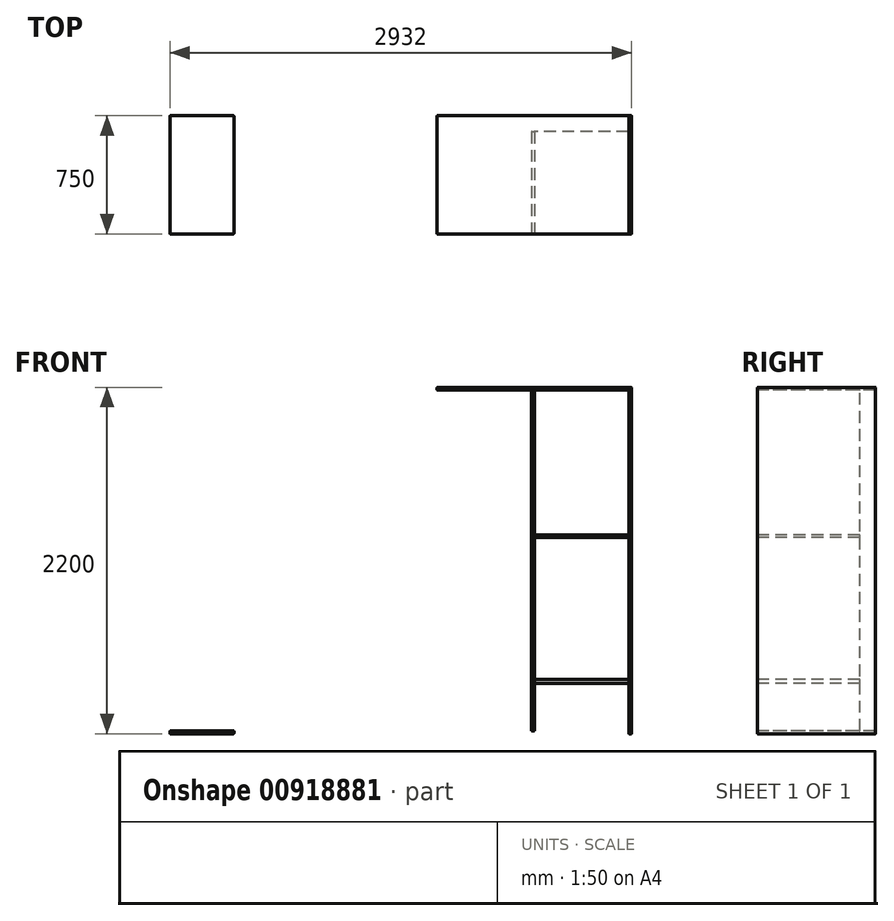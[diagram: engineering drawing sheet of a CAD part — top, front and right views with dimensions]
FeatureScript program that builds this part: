
annotation { "Feature Type Name" : "Feature", "Feature Type Description" : "" }
export const myFeature = defineFeature(function(context is Context, id is Id, definition is map)
    precondition{}
    {
        {
            var Q0;
            Q0=qCreatedBy(makeId("Front.planeOp"),FACE);
            var sketch = newSketch(context, id + "F0", { "sketchPlane" : qUnion([Q0])});
            skLineSegment(sketch, "E0.right", {"start": v(2950, 0) * mm, "end": v(2950, 2200) * mm});
            skLineSegment(sketch, "E1", {"start": v(1714, 2200) * mm, "end": v(1714, 0) * mm});
            skLineSegment(sketch, "E2", {"start": v(2332, 18) * mm, "end": v(2332, 2182) * mm});
            skLineSegment(sketch, "E3", {"start": v(1696, 0) * mm, "end": v(1696, 2200) * mm});
            skLineSegment(sketch, "E4", {"start": v(2932, 0) * mm, "end": v(2932, 2200) * mm});
            skLineSegment(sketch, "E5", {"start": v(2314, 18) * mm, "end": v(2314, 2182) * mm});
            skLineSegment(sketch, "E6", {"start": v(2932, 2200) * mm, "end": v(2950, 2200) * mm});
            skLineSegment(sketch, "E7", {"start": v(2932, 18) * mm, "end": v(1714, 18) * mm});
            skLineSegment(sketch, "E8", {"start": v(1714, 0) * mm, "end": v(2932, 0) * mm});
            skLineSegment(sketch, "E9", {"start": v(2932, 2200) * mm, "end": v(1714, 2200) * mm});
            skLineSegment(sketch, "E10", {"start": v(1714, 2182) * mm, "end": v(2932, 2182) * mm});
            skLineSegment(sketch, "E11", {"start": v(1714, 2200) * mm, "end": v(1696, 2200) * mm});
            skLineSegment(sketch, "E12", {"start": v(1714, 0) * mm, "end": v(1696, 0) * mm});
            skLineSegment(sketch, "E13", {"start": v(2932, 0) * mm, "end": v(2950, 0) * mm});
            skLineSegment(sketch, "E14", {"start": v(1714, 1264) * mm, "end": v(2314, 1264) * mm});
            skLineSegment(sketch, "E15", {"start": v(1714, 1246) * mm, "end": v(2314, 1246) * mm});
            skLineSegment(sketch, "E16", {"start": v(1714, 1362) * mm, "end": v(2314, 1362) * mm});
            skLineSegment(sketch, "E17", {"start": v(2932, 1344) * mm, "end": v(2332, 1344) * mm});
            skLineSegment(sketch, "E18.MirrorCS", {"start": v(1678, 2200) * mm, "end": v(1678, 0) * mm});
            skLineSegment(sketch, "E19.MirrorCS", {"start": v(1678, 0) * mm, "end": v(460, 0) * mm});
            skLineSegment(sketch, "E20.MirrorCS", {"start": v(460, 18) * mm, "end": v(1678, 18) * mm});
            skLineSegment(sketch, "E21.MirrorCS", {"start": v(1678, 2182) * mm, "end": v(460, 2182) * mm});
            skLineSegment(sketch, "E22.MirrorCS", {"start": v(460, 2200) * mm, "end": v(1678, 2200) * mm});
            skLineSegment(sketch, "E23.MirrorCS", {"start": v(1060, 18) * mm, "end": v(1060, 2182) * mm});
            skLineSegment(sketch, "E24.MirrorCS", {"start": v(1078, 18) * mm, "end": v(1078, 2182) * mm});
            skLineSegment(sketch, "E25.MirrorCS", {"start": v(460, 0) * mm, "end": v(460, 2200) * mm});
            skLineSegment(sketch, "E26.MirrorCS", {"start": v(1678, 0) * mm, "end": v(1696, 0) * mm});
            skLineSegment(sketch, "E27.MirrorCS", {"start": v(1678, 2200) * mm, "end": v(1696, 2200) * mm});
            skLineSegment(sketch, "E28", {"start": v(2932, 318) * mm, "end": v(2332, 318) * mm});
            skLineSegment(sketch, "E29", {"start": v(2332, 346) * mm, "end": v(2932, 346) * mm});
            skLineSegment(sketch, "E30", {"start": v(2314, 346) * mm, "end": v(1714, 346) * mm});
            skLineSegment(sketch, "E31", {"start": v(1714, 318) * mm, "end": v(2314, 318) * mm});
            skLineSegment(sketch, "E32", {"start": v(1678, 1344) * mm, "end": v(1078, 1344) * mm});
            skLineSegment(sketch, "E33", {"start": v(1678, 1362) * mm, "end": v(1078, 1362) * mm});
            skLineSegment(sketch, "E34", {"start": v(1678, 416) * mm, "end": v(1078, 416) * mm});
            skLineSegment(sketch, "E35", {"start": v(1060, 416) * mm, "end": v(460, 416) * mm});
            skLineSegment(sketch, "E36", {"start": v(1678, 318) * mm, "end": v(1078, 318) * mm});
            skLineSegment(sketch, "E37", {"start": v(1060, 318) * mm, "end": v(460, 318) * mm});
            skLineSegment(sketch, "E38", {"start": v(1678, 444) * mm, "end": v(1078, 444) * mm});
            skLineSegment(sketch, "E39", {"start": v(1060, 444) * mm, "end": v(460, 444) * mm});
            skLineSegment(sketch, "E40", {"start": v(1678, 336) * mm, "end": v(1078, 336) * mm});
            skLineSegment(sketch, "E41", {"start": v(1060, 336) * mm, "end": v(460, 336) * mm});
            skLineSegment(sketch, "E42", {"start": v(442, 2200) * mm, "end": v(442, 0) * mm});
            skLineSegment(sketch, "E43", {"start": v(424, 0) * mm, "end": v(424, 2200) * mm});
            skLineSegment(sketch, "E44", {"start": v(0, 0) * mm, "end": v(424, 0) * mm});
            skLineSegment(sketch, "E45", {"start": v(0, 2200) * mm, "end": v(424, 2200) * mm});
            skLineSegment(sketch, "E46", {"start": v(424, 2182) * mm, "end": v(18, 2182) * mm});
            skLineSegment(sketch, "E47", {"start": v(424, 2200) * mm, "end": v(442, 2200) * mm});
            skLineSegment(sketch, "E48", {"start": v(442, 0) * mm, "end": v(424, 0) * mm});
            skLineSegment(sketch, "E49", {"start": v(442, 0) * mm, "end": v(460, 0) * mm});
            skLineSegment(sketch, "E50", {"start": v(442, 2200) * mm, "end": v(460, 2200) * mm});
            skLineSegment(sketch, "E51", {"start": v(18, 2200) * mm, "end": v(18, 0) * mm});
            skLineSegment(sketch, "E52", {"start": v(0, 2200) * mm, "end": v(0, 0) * mm});
            skLineSegment(sketch, "E53", {"start": v(424, 18) * mm, "end": v(18, 18) * mm});
            skLineSegment(sketch, "E54.trimOffspring", {"start": v(2332, 1264) * mm, "end": v(2932, 1264) * mm});
            skLineSegment(sketch, "E55.trimOffspring", {"start": v(2332, 1246) * mm, "end": v(2932, 1246) * mm});
            skLineSegment(sketch, "E56.trimOffspring", {"start": v(2332, 1362) * mm, "end": v(2932, 1362) * mm});
            skLineSegment(sketch, "E57.trimOffspring", {"start": v(2314, 1344) * mm, "end": v(1714, 1344) * mm});
            skLineSegment(sketch, "E58.trimOffspring", {"start": v(1060, 1362) * mm, "end": v(460, 1362) * mm});
            skLineSegment(sketch, "E59.trimOffspring", {"start": v(1060, 1344) * mm, "end": v(460, 1344) * mm});
            skSolve(sketch);
        }
        {
            var Q0;
            Q0=makeQuery(id+"F0.imprint","IMPRINT",FACE,{"disambiguationData":[TD([[makeQuery(id+"F0.imprint","IMPRINT",EDGE,{"derivedFrom":sQuery(id+"F0.wireOp",EDGE,"E0.right")}),1.0]])]});
            extrude(context, id + "F1", {"entities" : qUnion([Q0]), "oppositeDirection" : true, "depth" : 750 * mm, "offsetDistance" : 25 * mm});
        }
        {
            var Q0;
            {var subQ0=sQuery(id+"F0.wireOp",EDGE,"E28");Q0=makeQuery(id+"F0.imprint","IMPRINT",FACE,{"disambiguationData":[TD([[makeQuery(id+"F0.imprint","IMPRINT",EDGE,{"derivedFrom":subQ0}),-1.0]])]});}
            extrude(context, id + "F2", {"entities" : qUnion([Q0]), "oppositeDirection" : true, "depth" : 650 * mm, "offsetDistance" : 25 * mm});
        }
        {
            var Q0;
            {var subQ0=sQuery(id+"F0.wireOp",EDGE,"E54.trimOffspring");Q0=makeQuery(id+"F0.imprint","IMPRINT",FACE,{"disambiguationData":[TD([[makeQuery(id+"F0.imprint","IMPRINT",EDGE,{"derivedFrom":subQ0}),-1.0]])]});}
            extrude(context, id + "F3", {"entities" : qUnion([Q0]), "oppositeDirection" : true, "depth" : 650 * mm, "offsetDistance" : 25 * mm});
        }
        {
            var Q0;
            {var subQ4=sQuery(id+"F0.wireOp",EDGE,"E9");Q0=makeQuery(id+"F0.imprint","IMPRINT",FACE,{"disambiguationData":[TD([[makeQuery(id+"F0.imprint","IMPRINT",EDGE,{"derivedFrom":subQ4}),1.0]])]});}
            extrude(context, id + "F4", {"entities" : qUnion([Q0]), "oppositeDirection" : true, "depth" : 750 * mm, "offsetDistance" : 25 * mm});
        }
        {
            var Q0;
            {var subQ4=sQuery(id+"F0.wireOp",EDGE,"E7");var subQ7=sQuery(id+"F0.wireOp",EDGE,"E2");var subQ12=makeQuery(id+"F0.imprint","INTERSECT",VERTEX,{"derivedFrom":[subQ7,subQ4]});Q0=makeQuery(id+"F0.imprint","IMPRINT",FACE,{"disambiguationData":[TD([[makeQuery(id+"F0.imprint","IMPRINT",EDGE,{"disambiguationData":[TD([[subQ12,-1.0]])],"derivedFrom":subQ7}),1.0]])]});}
            extrude(context, id + "F5", {"entities" : qUnion([Q0]), "oppositeDirection" : true, "depth" : 650 * mm, "offsetDistance" : 25 * mm});
        }
        {
            var Q0;
            {var subQ3=sQuery(id+"F0.wireOp",EDGE,"E53");Q0=makeQuery(id+"F0.imprint","IMPRINT",FACE,{"disambiguationData":[TD([[makeQuery(id+"F0.imprint","IMPRINT",EDGE,{"derivedFrom":subQ3}),1.0]])]});}
            extrude(context, id + "F6", {"entities" : qUnion([Q0]), "oppositeDirection" : true, "depth" : 750 * mm, "offsetDistance" : 25 * mm});
        }
        {
            var Q0;
            Q0=makeQuery(id+"F4.opExtrude","CAP_EDGE",EDGE,{"disambiguationData":[OSD([sQuery(id+"F0.wireOp",EDGE,"E9")])],"isStart":false});
            var Q1;
            Q1=makeQuery(id+"F4.opExtrude","SWEPT_EDGE",EDGE,{"disambiguationData":[OSD([sQuery(id+"F0.wireOp",EDGE,"E1"),sQuery(id+"F0.wireOp",EDGE,"E9"),sQuery(id+"F0.wireOp",EDGE,"E11")])]});
            var Q2;
            Q2=makeQuery(id+"F4.opExtrude","CAP_EDGE",EDGE,{"disambiguationData":[OSD([sQuery(id+"F0.wireOp",EDGE,"E10")])],"isStart":false});
            var Q3;
            Q3=makeQuery(id+"F4.opExtrude","SWEPT_EDGE",EDGE,{"disambiguationData":[OSD([sQuery(id+"F0.wireOp",EDGE,"E1"),sQuery(id+"F0.wireOp",EDGE,"E10")])]});
            var Q4;
            Q4=makeQuery(id+"F4.opExtrude","CAP_EDGE",EDGE,{"disambiguationData":[OSD([sQuery(id+"F0.wireOp",EDGE,"E9")])],"isStart":true});
            var Q5;
            Q5=makeQuery(id+"F4.opExtrude","CAP_EDGE",EDGE,{"disambiguationData":[OSD([sQuery(id+"F0.wireOp",EDGE,"E10")])],"isStart":true});
            var Q6;
            Q6=makeQuery(id+"F4.opExtrude","CAP_EDGE",EDGE,{"disambiguationData":[OSD([sQuery(id+"F0.wireOp",EDGE,"E1")])],"isStart":true});
            var Q7;
            Q7=makeQuery(id+"F4.opExtrude","CAP_EDGE",EDGE,{"disambiguationData":[OSD([sQuery(id+"F0.wireOp",EDGE,"E1")])],"isStart":false});
            var Q8;
            Q8=makeQuery(id+"F4.opExtrude","SWEPT_EDGE",EDGE,{"disambiguationData":[OSD([sQuery(id+"F0.wireOp",EDGE,"E4"),sQuery(id+"F0.wireOp",EDGE,"E6"),sQuery(id+"F0.wireOp",EDGE,"E9")])]});
            var Q9;
            Q9=makeQuery(id+"F4.opExtrude","CAP_EDGE",EDGE,{"disambiguationData":[OSD([sQuery(id+"F0.wireOp",EDGE,"E4")])],"isStart":false});
            var Q10;
            Q10=makeQuery(id+"F4.opExtrude","SWEPT_EDGE",EDGE,{"disambiguationData":[OSD([sQuery(id+"F0.wireOp",EDGE,"E4"),sQuery(id+"F0.wireOp",EDGE,"E10")])]});
            var Q11;
            Q11=makeQuery(id+"F4.opExtrude","CAP_EDGE",EDGE,{"disambiguationData":[OSD([sQuery(id+"F0.wireOp",EDGE,"E4")])],"isStart":true});
            fillet(context, id + "F7", {"entities" : qUnion([Q0, Q1, Q2, Q3, Q4, Q5, Q6, Q7, Q8, Q9, Q10, Q11]), "radius" : 2 * mm, "tangentPropagation" : true, "allowEdgeOverflow" : false});
        }
        {
            var Q0;
            Q0=makeQuery(id+"F1.opExtrude","SWEPT_EDGE",EDGE,{"disambiguationData":[OSD([sQuery(id+"F0.wireOp",EDGE,"E0.right"),sQuery(id+"F0.wireOp",EDGE,"E6")])]});
            var Q1;
            Q1=makeQuery(id+"F1.opExtrude","CAP_EDGE",EDGE,{"disambiguationData":[OSD([sQuery(id+"F0.wireOp",EDGE,"E6")])],"isStart":true});
            var Q2;
            Q2=makeQuery(id+"F1.opExtrude","CAP_EDGE",EDGE,{"disambiguationData":[OSD([sQuery(id+"F0.wireOp",EDGE,"E0.right")])],"isStart":true});
            var Q3;
            Q3=makeQuery(id+"F1.opExtrude","CAP_EDGE",EDGE,{"disambiguationData":[OSD([sQuery(id+"F0.wireOp",EDGE,"E4")])],"isStart":true});
            var Q4;
            Q4=makeQuery(id+"F1.opExtrude","SWEPT_EDGE",EDGE,{"disambiguationData":[OSD([sQuery(id+"F0.wireOp",EDGE,"E4"),sQuery(id+"F0.wireOp",EDGE,"E6"),sQuery(id+"F0.wireOp",EDGE,"E9")])]});
            var Q5;
            Q5=makeQuery(id+"F1.opExtrude","CAP_EDGE",EDGE,{"disambiguationData":[OSD([sQuery(id+"F0.wireOp",EDGE,"E0.right")])],"isStart":false});
            var Q6;
            Q6=makeQuery(id+"F1.opExtrude","CAP_EDGE",EDGE,{"disambiguationData":[OSD([sQuery(id+"F0.wireOp",EDGE,"E4")])],"isStart":false});
            var Q7;
            Q7=makeQuery(id+"F1.opExtrude","CAP_EDGE",EDGE,{"disambiguationData":[OSD([sQuery(id+"F0.wireOp",EDGE,"E6")])],"isStart":false});
            var Q8;
            Q8=makeQuery(id+"F1.opExtrude","CAP_EDGE",EDGE,{"disambiguationData":[OSD([sQuery(id+"F0.wireOp",EDGE,"E13")])],"isStart":false});
            var Q9;
            Q9=makeQuery(id+"F1.opExtrude","SWEPT_EDGE",EDGE,{"disambiguationData":[OSD([sQuery(id+"F0.wireOp",EDGE,"E0.right"),sQuery(id+"F0.wireOp",EDGE,"E13")])]});
            var Q10;
            Q10=makeQuery(id+"F1.opExtrude","SWEPT_EDGE",EDGE,{"disambiguationData":[OSD([sQuery(id+"F0.wireOp",EDGE,"E4"),sQuery(id+"F0.wireOp",EDGE,"E8"),sQuery(id+"F0.wireOp",EDGE,"E13")])]});
            var Q11;
            Q11=makeQuery(id+"F1.opExtrude","CAP_EDGE",EDGE,{"disambiguationData":[OSD([sQuery(id+"F0.wireOp",EDGE,"E13")])],"isStart":true});
            var Q12;
            Q12=makeQuery(id+"F5.opExtrude","SWEPT_EDGE",EDGE,{"disambiguationData":[OSD([sQuery(id+"F0.wireOp",EDGE,"E2"),sQuery(id+"F0.wireOp",EDGE,"E7")])]});
            var Q13;
            Q13=makeQuery(id+"F5.opExtrude","CAP_EDGE",EDGE,{"disambiguationData":[OSD([sQuery(id+"F0.wireOp",EDGE,"E7")])],"isStart":true});
            var Q14;
            Q14=makeQuery(id+"F5.opExtrude","CAP_EDGE",EDGE,{"disambiguationData":[OSD([sQuery(id+"F0.wireOp",EDGE,"E5")])],"isStart":true});
            var Q15;
            Q15=makeQuery(id+"F5.opExtrude","SWEPT_EDGE",EDGE,{"disambiguationData":[OSD([sQuery(id+"F0.wireOp",EDGE,"E5"),sQuery(id+"F0.wireOp",EDGE,"E7")])]});
            var Q16;
            Q16=makeQuery(id+"F5.opExtrude","CAP_EDGE",EDGE,{"disambiguationData":[OSD([sQuery(id+"F0.wireOp",EDGE,"E2")])],"isStart":true});
            var Q17;
            Q17=makeQuery(id+"F5.opExtrude","CAP_EDGE",EDGE,{"disambiguationData":[OSD([sQuery(id+"F0.wireOp",EDGE,"E7")])],"isStart":false});
            var Q18;
            Q18=makeQuery(id+"F5.opExtrude","CAP_EDGE",EDGE,{"disambiguationData":[OSD([sQuery(id+"F0.wireOp",EDGE,"E5")])],"isStart":false});
            var Q19;
            Q19=makeQuery(id+"F5.opExtrude","CAP_EDGE",EDGE,{"disambiguationData":[OSD([sQuery(id+"F0.wireOp",EDGE,"E2")])],"isStart":false});
            var Q20;
            Q20=makeQuery(id+"F5.opExtrude","CAP_EDGE",EDGE,{"disambiguationData":[OSD([sQuery(id+"F0.wireOp",EDGE,"E10")])],"isStart":false});
            var Q21;
            Q21=makeQuery(id+"F5.opExtrude","SWEPT_EDGE",EDGE,{"disambiguationData":[OSD([sQuery(id+"F0.wireOp",EDGE,"E5"),sQuery(id+"F0.wireOp",EDGE,"E10")])]});
            var Q22;
            Q22=makeQuery(id+"F5.opExtrude","SWEPT_EDGE",EDGE,{"disambiguationData":[OSD([sQuery(id+"F0.wireOp",EDGE,"E2"),sQuery(id+"F0.wireOp",EDGE,"E10")])]});
            var Q23;
            Q23=makeQuery(id+"F5.opExtrude","CAP_EDGE",EDGE,{"disambiguationData":[OSD([sQuery(id+"F0.wireOp",EDGE,"E10")])],"isStart":true});
            fillet(context, id + "F8", {"entities" : qUnion([Q0, Q1, Q2, Q3, Q4, Q5, Q6, Q7, Q8, Q9, Q10, Q11, Q12, Q13, Q14, Q15, Q16, Q17, Q18, Q19, Q20, Q21, Q22, Q23]), "radius" : 2 * mm, "tangentPropagation" : true, "allowEdgeOverflow" : false});
        }
        {
            var Q0;
            Q0=makeQuery(id+"F2.opExtrude","CAP_EDGE",EDGE,{"disambiguationData":[OSD([sQuery(id+"F0.wireOp",EDGE,"E28")])],"isStart":true});
            var Q1;
            Q1=makeQuery(id+"F2.opExtrude","CAP_EDGE",EDGE,{"disambiguationData":[OSD([sQuery(id+"F0.wireOp",EDGE,"E29")])],"isStart":true});
            var Q2;
            Q2=makeQuery(id+"F2.opExtrude","CAP_EDGE",EDGE,{"disambiguationData":[OSD([sQuery(id+"F0.wireOp",EDGE,"E2")])],"isStart":true});
            var Q3;
            Q3=makeQuery(id+"F2.opExtrude","SWEPT_EDGE",EDGE,{"disambiguationData":[OSD([sQuery(id+"F0.wireOp",EDGE,"E2"),sQuery(id+"F0.wireOp",EDGE,"E29")])]});
            var Q4;
            Q4=makeQuery(id+"F2.opExtrude","SWEPT_EDGE",EDGE,{"disambiguationData":[OSD([sQuery(id+"F0.wireOp",EDGE,"E2"),sQuery(id+"F0.wireOp",EDGE,"E28")])]});
            var Q5;
            Q5=makeQuery(id+"F2.opExtrude","CAP_EDGE",EDGE,{"disambiguationData":[OSD([sQuery(id+"F0.wireOp",EDGE,"E29")])],"isStart":false});
            var Q6;
            Q6=makeQuery(id+"F2.opExtrude","CAP_EDGE",EDGE,{"disambiguationData":[OSD([sQuery(id+"F0.wireOp",EDGE,"E28")])],"isStart":false});
            var Q7;
            Q7=makeQuery(id+"F2.opExtrude","CAP_EDGE",EDGE,{"disambiguationData":[OSD([sQuery(id+"F0.wireOp",EDGE,"E2")])],"isStart":false});
            var Q8;
            Q8=makeQuery(id+"F2.opExtrude","SWEPT_EDGE",EDGE,{"disambiguationData":[OSD([sQuery(id+"F0.wireOp",EDGE,"E4"),sQuery(id+"F0.wireOp",EDGE,"E29")])]});
            var Q9;
            Q9=makeQuery(id+"F2.opExtrude","CAP_EDGE",EDGE,{"disambiguationData":[OSD([sQuery(id+"F0.wireOp",EDGE,"E4")])],"isStart":false});
            var Q10;
            Q10=makeQuery(id+"F2.opExtrude","SWEPT_EDGE",EDGE,{"disambiguationData":[OSD([sQuery(id+"F0.wireOp",EDGE,"E4"),sQuery(id+"F0.wireOp",EDGE,"E28")])]});
            var Q11;
            Q11=makeQuery(id+"F2.opExtrude","CAP_EDGE",EDGE,{"disambiguationData":[OSD([sQuery(id+"F0.wireOp",EDGE,"E4")])],"isStart":true});
            fillet(context, id + "F9", {"entities" : qUnion([Q0, Q1, Q2, Q3, Q4, Q5, Q6, Q7, Q8, Q9, Q10, Q11]), "radius" : 2 * mm, "tangentPropagation" : true, "allowEdgeOverflow" : false});
        }
        {
            var Q0;
            Q0=makeQuery(id+"F3.opExtrude","CAP_FACE",FACE,{"disambiguationData":[OSD([sQuery(id+"F0.wireOp",EDGE,"E2"),sQuery(id+"F0.wireOp",EDGE,"E4"),sQuery(id+"F0.wireOp",EDGE,"E54.trimOffspring"),sQuery(id+"F0.wireOp",EDGE,"E55.trimOffspring")])],"isStart":false});
            var Q1;
            Q1=makeQuery(id+"F3.opExtrude","SWEPT_FACE",FACE,{"disambiguationData":[OSD([sQuery(id+"F0.wireOp",EDGE,"E4")])]});
            var Q2;
            Q2=makeQuery(id+"F3.opExtrude","SWEPT_FACE",FACE,{"disambiguationData":[OSD([sQuery(id+"F0.wireOp",EDGE,"E2")])]});
            var Q3;
            Q3=makeQuery(id+"F3.opExtrude","CAP_FACE",FACE,{"disambiguationData":[OSD([sQuery(id+"F0.wireOp",EDGE,"E2"),sQuery(id+"F0.wireOp",EDGE,"E4"),sQuery(id+"F0.wireOp",EDGE,"E54.trimOffspring"),sQuery(id+"F0.wireOp",EDGE,"E55.trimOffspring")])],"isStart":true});
            fillet(context, id + "F10", {"entities" : qUnion([Q0, Q1, Q2, Q3]), "radius" : 2 * mm, "tangentPropagation" : true, "allowEdgeOverflow" : false});
        }
        {
            var Q0;
            Q0=makeQuery(id+"F6.opExtrude","SWEPT_FACE",FACE,{"disambiguationData":[OSD([sQuery(id+"F0.wireOp",EDGE,"E51")])]});
            var Q1;
            Q1=makeQuery(id+"F6.opExtrude","CAP_FACE",FACE,{"disambiguationData":[OSD([sQuery(id+"F0.wireOp",EDGE,"E43"),sQuery(id+"F0.wireOp",EDGE,"E44"),sQuery(id+"F0.wireOp",EDGE,"E51"),sQuery(id+"F0.wireOp",EDGE,"E53")])],"isStart":false});
            var Q2;
            Q2=makeQuery(id+"F6.opExtrude","SWEPT_FACE",FACE,{"disambiguationData":[OSD([sQuery(id+"F0.wireOp",EDGE,"E43")])]});
            var Q3;
            Q3=makeQuery(id+"F6.opExtrude","SWEPT_FACE",FACE,{"disambiguationData":[OSD([sQuery(id+"F0.wireOp",EDGE,"E44")])]});
            var Q4;
            Q4=makeQuery(id+"F6.opExtrude","CAP_FACE",FACE,{"disambiguationData":[OSD([sQuery(id+"F0.wireOp",EDGE,"E43"),sQuery(id+"F0.wireOp",EDGE,"E44"),sQuery(id+"F0.wireOp",EDGE,"E51"),sQuery(id+"F0.wireOp",EDGE,"E53")])],"isStart":true});
            fillet(context, id + "F11", {"entities" : qUnion([Q0, Q1, Q2, Q3, Q4]), "radius" : 2 * mm, "tangentPropagation" : true, "allowEdgeOverflow" : false});
        }
    });
